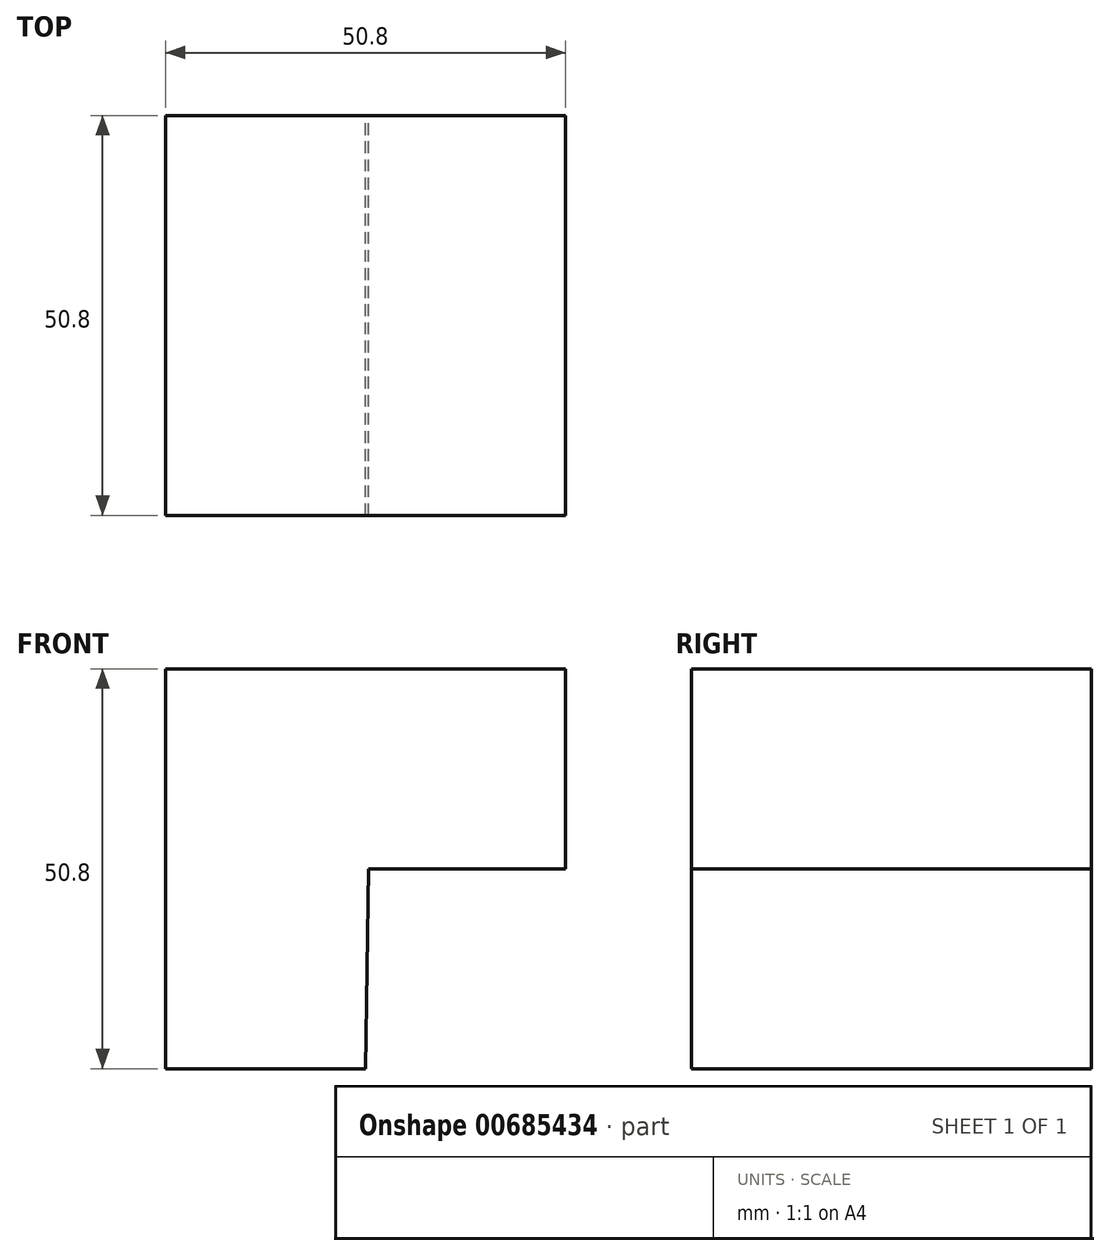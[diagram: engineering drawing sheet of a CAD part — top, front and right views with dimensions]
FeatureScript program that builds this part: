
annotation { "Feature Type Name" : "Feature", "Feature Type Description" : "" }
export const myFeature = defineFeature(function(context is Context, id is Id, definition is map)
    precondition{}
    {
        {
            var Q0;
            Q0=qCreatedBy(makeId("Front.planeOp"),FACE);
            var sketch = newSketch(context, id + "F0", { "sketchPlane" : qUnion([Q0])});
            skLineSegment(sketch, "E0", {"start": v(-50.8, 0) * mm, "end": v(-25.4, 0) * mm});
            skLineSegment(sketch, "E1", {"start": v(-50.8, 0) * mm, "end": v(-50.8, 50.8) * mm});
            skLineSegment(sketch, "E2", {"start": v(-50.8, 50.8) * mm, "end": v(0, 50.8) * mm});
            skLineSegment(sketch, "E3", {"start": v(0, 50.8) * mm, "end": v(0, 25.4) * mm});
            skLineSegment(sketch, "E4", {"start": v(0, 25.4) * mm, "end": v(-18.4, 25.4) * mm});
            skLineSegment(sketch, "E5", {"start": v(-18.4, 25.4) * mm, "end": v(-25.05, 25.4) * mm});
            skLineSegment(sketch, "E6", {"start": v(-25.05, 25.4) * mm, "end": v(-25.4, 0) * mm});
            skSolve(sketch);
        }
        {
            var Q0;
            Q0=makeQuery(id+"F0.imprint","IMPRINT",FACE,{"disambiguationData":[TD([[makeQuery(id+"F0.imprint","IMPRINT",EDGE,{"derivedFrom":sQuery(id+"F0.wireOp",EDGE,"E0")}),1.0]])]});
            extrude(context, id + "F1", {"entities" : qUnion([Q0]), "depth" : 50.8 * mm, "offsetDistance" : 25.4 * mm});
        }
    });
